# Revit family: Appliance_Cabinet-Danver-Double_Warming_Drawer
name_source: partatom
category: Casework
units: mm (PartAtom-declared; Revit-internal decimal feet)

## family parameters
Always vertical = Yes
Classification Number = 23.40.35.17.47
Cut with Voids When Loaded = No
Room Calculation Point = No
Shared = No
Work Plane-Based = No

## types (4) — shared parameters
Cabinet Material = Metal - Danver - Stainless Steel
Construction Type = 304 Grade Stainless Steel
Default Elevation = 0' - 0"
Handle Material = Metal - Danver - Chrome Plated Steel
Height = 2' - 6"
Keynote = 12 35 28
Manufacturer = Danver Outdoor Kitchens
Manufacturer Note = Generic Warming Drawer shown, contact Danver for more information
Product Documentation Link = https://danver.com
Product Name = Base Cabinet - Danver - Double Warming Drawer
Product Page URL = https://danver.com
Toe Height = 0' - 4 1/2"
Toe Kick Material = Metal - Danver - Toe Kick
URL = www.danver.com
Version = 2019 - V1.0b

## per-type parameters (varying)
| type | Depth | Depth+Door | Description | Model | Width |
| 30" Width - 27" Depth | 2' - 3" | 2' - 3 7/8" | 30"x27"D Double Warming Drawer Base | OWD3000 | 2' - 6" |
| 30" Width - 24" Depth | 2' - 0" | 2' - 0 7/8" | 33"x27"D Double Warming Drawer Base | OWD3000-24 | 2' - 6" |
| 33" Width - 27" Depth | 2' - 3" | 2' - 3 7/8" | 33"x24"D Double Warming Drawer Base | OWD3300 | 2' - 9" |
| 33" Width - 24" Depth | 2' - 0" | 2' - 0 7/8" | 30"x24"D Double Warming Drawer Base | OWD3300-24 | 2' - 9" |

## geometry (parser evidence)
native form markers: Sweep x32
no freeform markers — native parametric forms only
